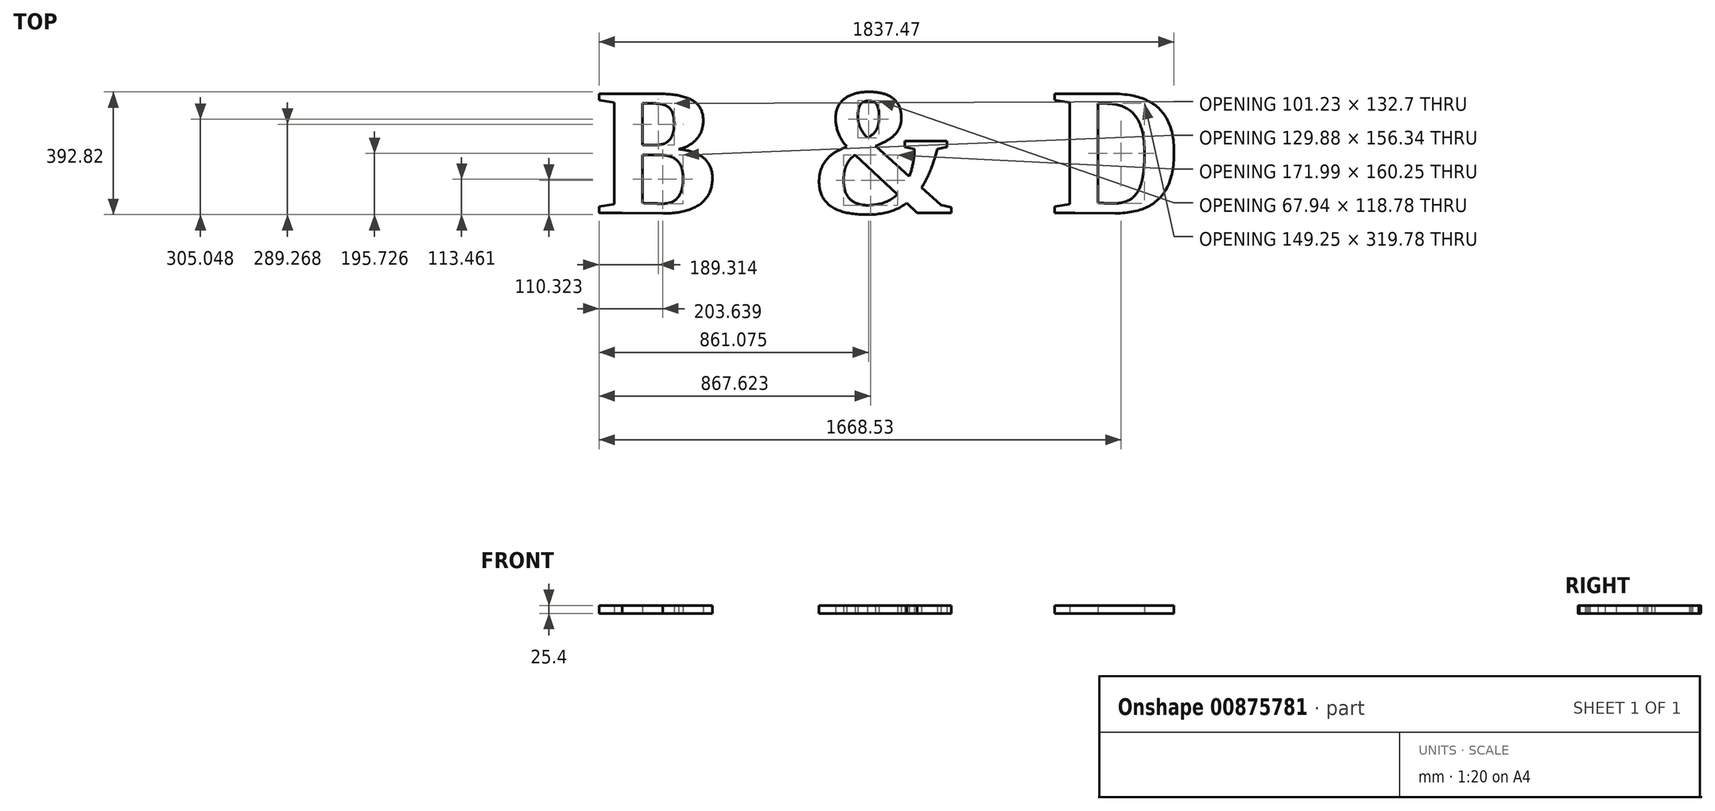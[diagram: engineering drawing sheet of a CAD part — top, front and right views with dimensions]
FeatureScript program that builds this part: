
annotation { "Feature Type Name" : "Feature", "Feature Type Description" : "" }
export const myFeature = defineFeature(function(context is Context, id is Id, definition is map)
    precondition{}
    {
        {
            var Q0;
            Q0=qCreatedBy(makeId("Top.planeOp"),FACE);
            var sketch = newSketch(context, id + "F0", { "sketchPlane" : qUnion([Q0])});
            skText(sketch, "E0", { "text": "B  &  D", "fontName": "Tinos-Bold.ttf"});
            skLineSegment(sketch, "E1", {"start": v(442.96, -36.75) * mm, "end": v(823.96, -36.75) * mm, "construction": true});
            const initialGuessF0  = {"E0": [0, 0, 1, 0, 0.4191]};
            skSetInitialGuess(sketch, initialGuessF0);
            skSolve(sketch);
        }
        {
            var Q0;
            Q0 = qSketchRegion(id + "F0", true);
            extrude(context, id + "F1", {"entities" : qUnion([Q0]), "depth" : 25.4 * mm, "offsetDistance" : 25.4 * mm});
        }
    });
